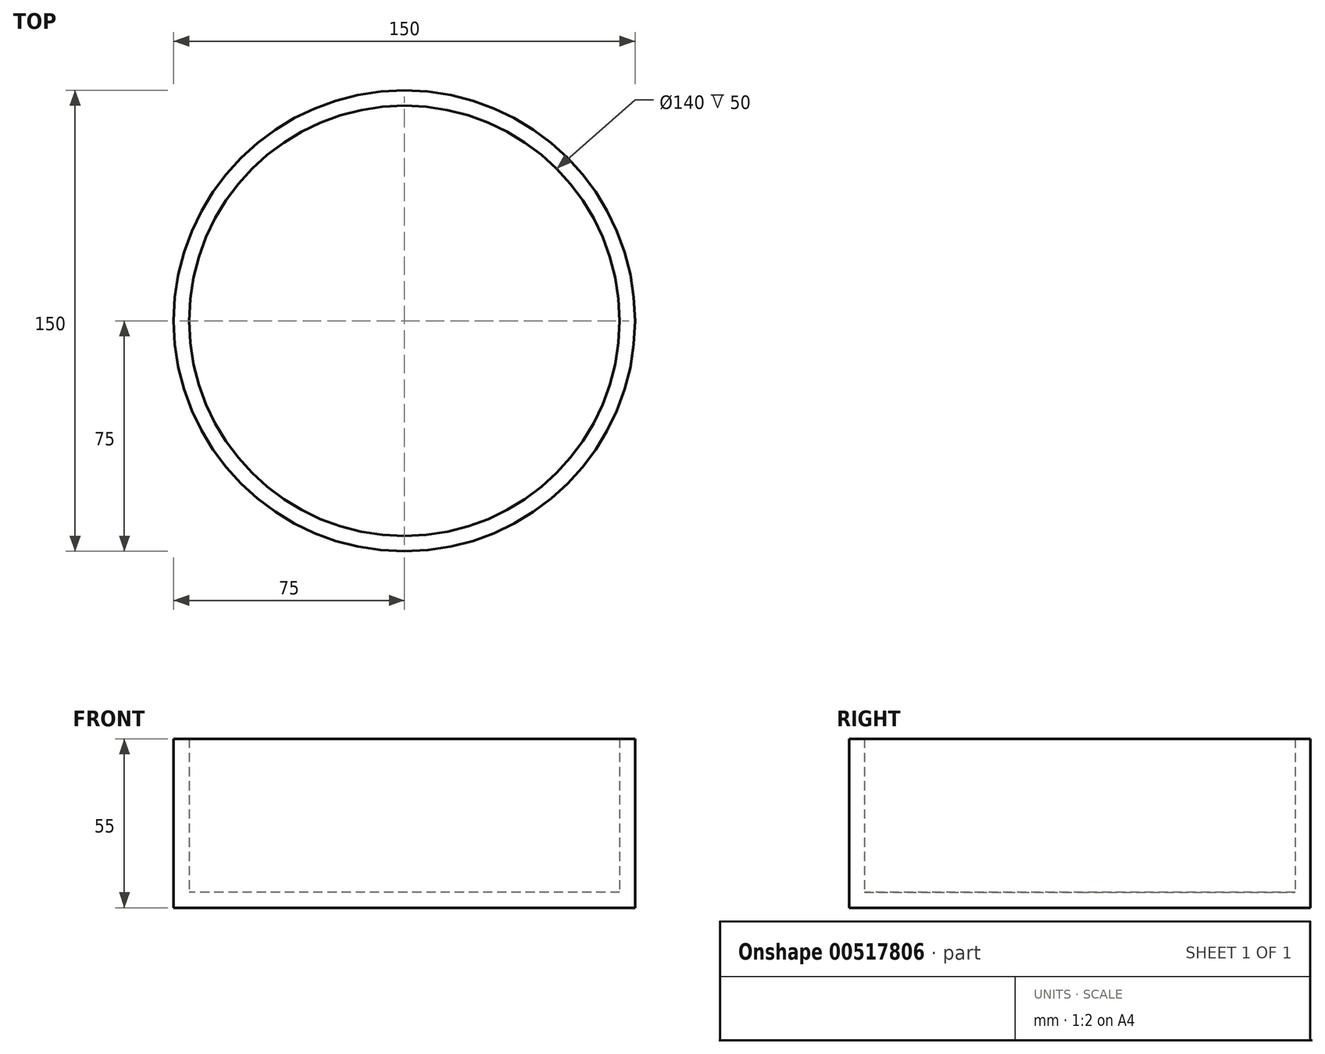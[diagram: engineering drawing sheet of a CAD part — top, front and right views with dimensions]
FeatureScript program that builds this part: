
annotation { "Feature Type Name" : "Feature", "Feature Type Description" : "" }
export const myFeature = defineFeature(function(context is Context, id is Id, definition is map)
    precondition{}
    {
        {
            var Q0;
            Q0=qCreatedBy(makeId("Top.planeOp"),FACE);
            var sketch = newSketch(context, id + "F0", { "sketchPlane" : qUnion([Q0])});
            skCircle(sketch, "E0", {"center": v(0, 0) * mm, "radius": 75 * mm});
            skSolve(sketch);
        }
        {
            var Q0;
            Q0=makeQuery(id+"F0.imprint","IMPRINT",FACE,{"disambiguationData":[TD([[makeQuery(id+"F0.imprint","IMPRINT",EDGE,{"derivedFrom":sQuery(id+"F0.wireOp",EDGE,"E0")}),1.0]])]});
            extrude(context, id + "F1", {"entities" : qUnion([Q0]), "depth" : 5 * mm, "offsetDistance" : 25 * mm});
        }
        {
            var Q0;
            Q0=makeQuery(id+"F1.opExtrude","CAP_FACE",FACE,{"disambiguationData":[OSD([sQuery(id+"F0.wireOp",EDGE,"E0")])],"isStart":false});
            var sketch = newSketch(context, id + "F2", { "sketchPlane" : qUnion([Q0])});
            skCircle(sketch, "E1", {"center": v(0, 0) * mm, "radius": 75 * mm});
            skCircle(sketch, "E2", {"center": v(0, 0) * mm, "radius": 70 * mm});
            skSolve(sketch);
        }
        {
            var Q0;
            Q0 = qSketchRegion(id + "F2", true);
            extrude(context, id + "F3", {"entities" : qUnion([Q0]), "operationType" : NewBodyOperationType.ADD, "depth" : 50 * mm, "offsetDistance" : 25 * mm});
        }
    });
